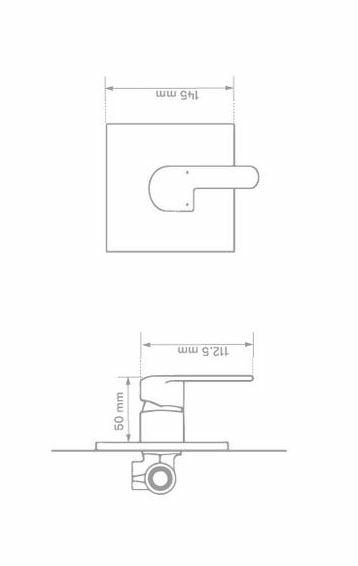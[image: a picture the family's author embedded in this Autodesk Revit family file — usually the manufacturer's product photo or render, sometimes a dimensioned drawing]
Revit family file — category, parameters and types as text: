
# Revit family: 01-0846-11SR MEZCLADOR DUCHA 8” 3 LLAVES SIN SALIDA CALIMA
name_source: partatom
category: Aparatos sanitarios
revit_build: Autodesk Revit 2018 (Build: 20170223_1515(x64)
units: mm (PartAtom-declared; Revit-internal decimal feet)

## family parameters
Anfitrión = Cara
Compartido = No
Corte con vacíos al cargar = No
Cota de conector redondo = Diámetro de uso
Número OmniClass = 23.31.11.00
Punto de cálculo de habitación = No
Tipo de pieza = Normal

## types (1)
- 01-0846-11SR
    Altura manija = 85 mm  [stored 0.278871 ft]
    Ancho escudo = 60 mm  [stored 0.19685 ft]
    Conexión AC = Sí
    Conexión AF = Sí
    Conexión de residuos = No
    Conexión de ventilación = No
    Descripción = Mezclador ducha
    Distancia entre griferias = 203.2 mm
    Elevación por defecto = 0 mm  [stored 0 ft]
    Fabricante = Gricol
    Imagen de tipo = Captura.PNG
    Link Ficha Tecnica = No encontrada en internet
    Manija = 72 mm  [stored 0.23622 ft]
    Manija simple = 75 mm
    Metal Zamak Cromado = Metal Zamak Cromado
    Modelo = 01-0846-11SR
    Plastico ABS Cromado = Plastico - ABS Cromado
    Product Name = MEZCLADOR DUCHA 8” 3 LLAVES SIN SALIDA CALIMA
    URL = https://www.gricol.com

note: [stored X ft] marks values corroborated as IEEE doubles in the binary element streams (Revit-internal decimal feet)

## geometry (parser evidence)
native form markers: Blend x2, Sweep x13
no freeform markers — native parametric forms only
